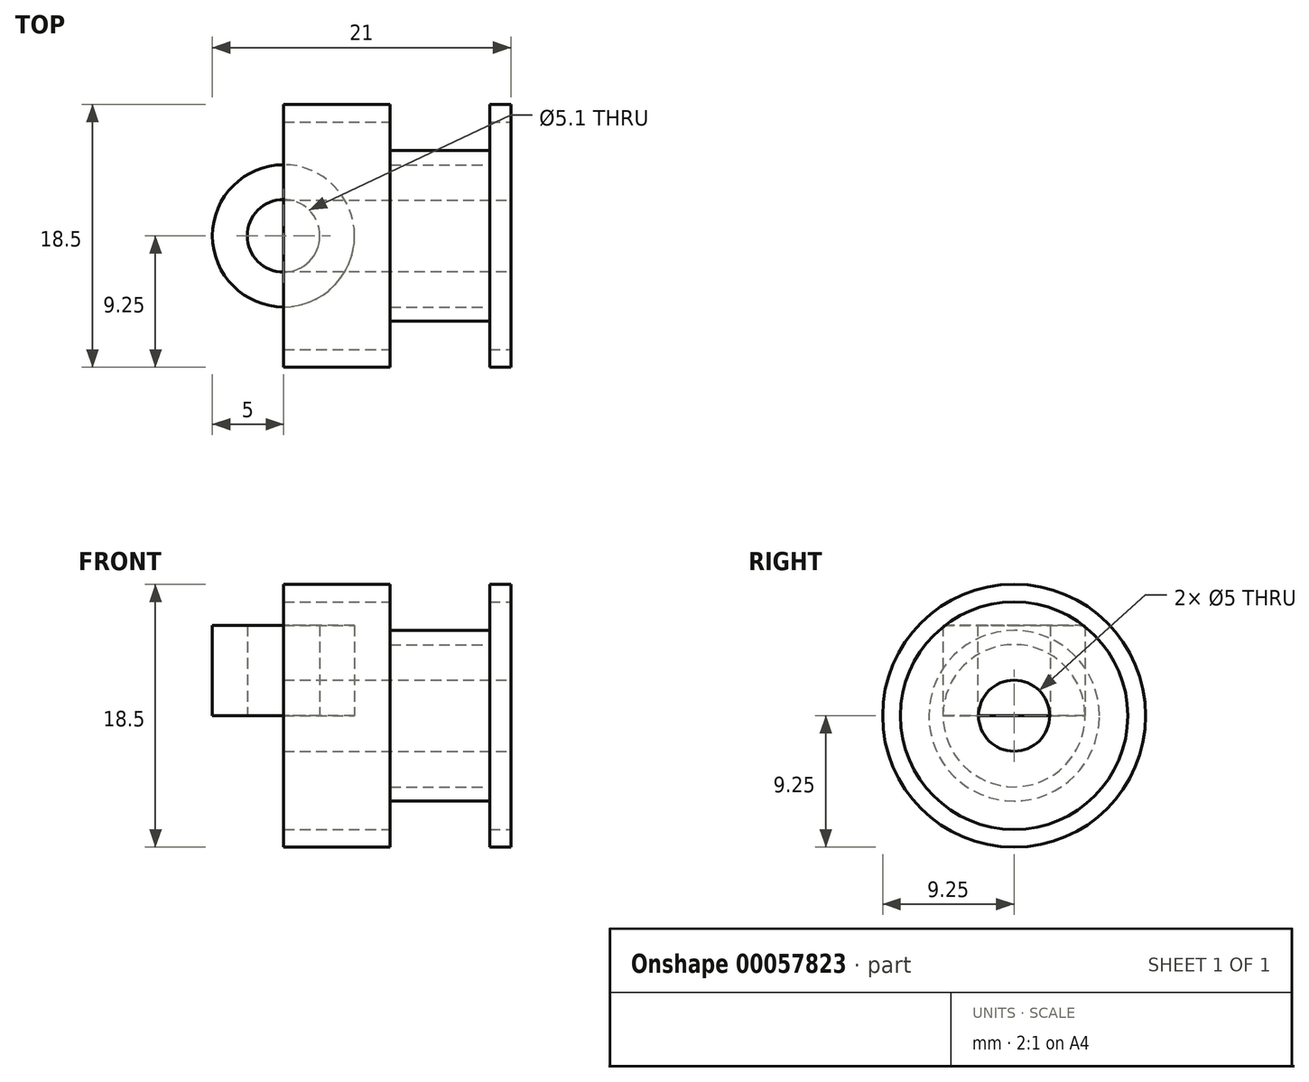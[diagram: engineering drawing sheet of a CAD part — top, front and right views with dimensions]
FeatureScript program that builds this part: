
annotation { "Feature Type Name" : "Feature", "Feature Type Description" : "" }
export const myFeature = defineFeature(function(context is Context, id is Id, definition is map)
    precondition{}
    {
        {
            var Q0;
            Q0=qCreatedBy(makeId("Top.planeOp"),FACE);
            var sketch = newSketch(context, id + "F0", { "sketchPlane" : qUnion([Q0])});
            skLineSegment(sketch, "E0", {"start": v(0, 0) * mm, "end": v(-38, 0) * mm});
            skLineSegment(sketch, "E1.bottom", {"start": v(0, 2.5) * mm, "end": v(16, 2.5) * mm});
            skLineSegment(sketch, "E1.top", {"start": v(0, 8) * mm, "end": v(16, 8) * mm});
            skLineSegment(sketch, "E1.left", {"start": v(0, 2.5) * mm, "end": v(0, 8) * mm});
            skLineSegment(sketch, "E1.right", {"start": v(16, 2.5) * mm, "end": v(16, 8) * mm});
            skLineSegment(sketch, "E2", {"start": v(7.5, 8) * mm, "end": v(7.5, 5) * mm});
            skLineSegment(sketch, "E3", {"start": v(7.5, 5) * mm, "end": v(14.5, 5) * mm});
            skLineSegment(sketch, "E4", {"start": v(14.5, 5) * mm, "end": v(14.5, 8) * mm});
            skSolve(sketch);
        }
        {
            var Q0;
            Q0=makeQuery(id+"F0.imprint","IMPRINT",FACE,{"disambiguationData":[TD([[makeQuery(id+"F0.imprint","IMPRINT",EDGE,{"derivedFrom":sQuery(id+"F0.wireOp",EDGE,"E1.bottom")}),1.0]])]});
            var Q1;
            Q1=sQuery(id+"F0.wireOp",EDGE,"E0");
            revolve(context, id + "F1", {"entities" : qUnion([Q0]), "axis" : qUnion([Q1]), "revolveType" : RevolveType.FULL});
        }
        {
            var Q0;
            Q0=qCreatedBy(makeId("Top.planeOp"),FACE);
            var sketch = newSketch(context, id + "F2", { "sketchPlane" : qUnion([Q0])});
            skLineSegment(sketch, "E5", {"start": v(49.31, 0) * mm, "end": v(0, 0) * mm});
            skLineSegment(sketch, "E6.bottom", {"start": v(0, 2.5) * mm, "end": v(16, 2.5) * mm});
            skLineSegment(sketch, "E6.top", {"start": v(0, 9.25) * mm, "end": v(16, 9.25) * mm});
            skLineSegment(sketch, "E6.left", {"start": v(0, 2.5) * mm, "end": v(0, 9.25) * mm});
            skLineSegment(sketch, "E6.right", {"start": v(16, 2.5) * mm, "end": v(16, 9.25) * mm});
            skLineSegment(sketch, "E7", {"start": v(7.5, 9.25) * mm, "end": v(7.5, 6) * mm});
            skLineSegment(sketch, "E8", {"start": v(7.5, 6) * mm, "end": v(14.5, 6) * mm});
            skLineSegment(sketch, "E9", {"start": v(14.5, 6) * mm, "end": v(14.5, 9.25) * mm});
            skSolve(sketch);
        }
        {
            var Q0;
            Q0=makeQuery(id+"F2.imprint","IMPRINT",FACE,{"disambiguationData":[TD([[makeQuery(id+"F2.imprint","IMPRINT",EDGE,{"derivedFrom":sQuery(id+"F2.wireOp",EDGE,"E6.bottom")}),1.0]])]});
            var Q1;
            Q1=sQuery(id+"F2.wireOp",EDGE,"E5");
            revolve(context, id + "F3", {"entities" : qUnion([Q0]), "axis" : qUnion([Q1]), "revolveType" : RevolveType.FULL});
        }
        {
            var Q0;
            Q0=qCreatedBy(makeId("Top.planeOp"),FACE);
            var sketch = newSketch(context, id + "F4", { "sketchPlane" : qUnion([Q0])});
            skCircle(sketch, "E10", {"center": v(0, 0) * mm, "radius": 5 * mm});
            skCircle(sketch, "E11", {"center": v(0, 0) * mm, "radius": 2.55 * mm});
            skSolve(sketch);
        }
        {
            var Q0;
            Q0=makeQuery(id+"F4.imprint","IMPRINT",FACE,{"disambiguationData":[TD([[makeQuery(id+"F4.imprint","IMPRINT",EDGE,{"derivedFrom":sQuery(id+"F4.wireOp",EDGE,"E10")}),1.0]])]});
            extrude(context, id + "F5", {"entities" : qUnion([Q0]), "depth" : 6.35 * mm, "offsetDistance" : 25 * mm});
        }
    });
